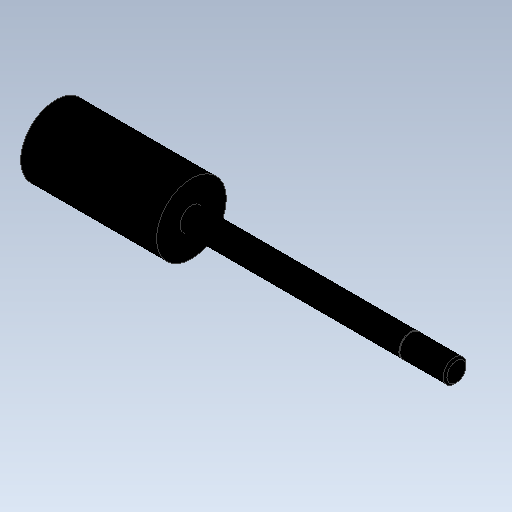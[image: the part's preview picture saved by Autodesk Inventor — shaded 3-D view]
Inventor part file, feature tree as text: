
AUTODESK INVENTOR PART (.ipt)
format: ipt  version: 2020 (Build 240168000, 168)  size: 123,904 bytes
history: native  units: mm (DEFAULTED — no unit token found)
features: other x70, revolve x3, sketch x3
ambient origin geometry x8: Origin, YZ Plane, XZ Plane, XY Plane, X Axis, Y Axis, Z Axis, Center Point
bodies: Solid1 (feature_tree)
feature tree (76):
  revolve  "Revolution1"  Angle=360.0deg
  revolve  "Revolution2"  [1 undecoded]
  revolve  "Revolution3"  [1 undecoded]
  other  "dia1_XY"
  other  "dia1_YZ"
  other  "dia1_ZX"
  other  "dia1_X"
  other  "dia1_Y"
  other  "dia1_Z"
  other  "dia1_Center"
  other  "dia12_XY"
  other  "dia12_YZ"
  other  "dia12_ZX"
  other  "dia12_X"
  other  "dia12_Y"
  other  "dia12_Z"
  other  "dia12_Center"
  other  "dia2_XY"
  other  "dia2_YZ"
  other  "dia2_ZX"
  other  "dia2_X"
  other  "dia2_Y"
  other  "dia2_Z"
  other  "dia2_Center"
  other  "dia22_XY"
  other  "dia22_YZ"
  other  "dia22_ZX"
  other  "dia22_X"
  other  "dia22_Y"
  other  "dia22_Z"
  other  "dia22_Center"
  other  "rl1_XY"
  other  "rl1_YZ"
  other  "rl1_ZX"
  other  "rl1_X"
  other  "rl1_Y"
  other  "rl1_Z"
  other  "rl1_Center"
  other  "rl2_XY"
  other  "rl2_YZ"
  other  "rl2_ZX"
  other  "rl2_X"
  other  "rl2_Y"
  other  "rl2_Z"
  other  "rl2_Center"
  other  "rod_cp_XY"
  other  "rod_cp_YZ"
  other  "rod_cp_ZX"
  other  "rod_cp_X"
  other  "rod_cp_Y"
  other  "rod_cp_Z"
  other  "rod_cp_Center"
  other  "thd1_XY"
  other  "thd1_YZ"
  other  "thd1_ZX"
  other  "thd1_X"
  other  "thd1_Y"
  other  "thd1_Z"
  other  "thd1_Center"
  other  "thd2_XY"
  other  "thd2_YZ"
  other  "thd2_ZX"
  other  "thd2_X"
  other  "thd2_Y"
  other  "thd2_Z"
  other  "thd2_Center"
  other  "to_rod_clevis_XY"
  other  "to_rod_clevis_YZ"
  other  "to_rod_clevis_ZX"
  other  "to_rod_clevis_X"
  other  "to_rod_clevis_Y"
  other  "to_rod_clevis_Z"
  other  "to_rod_clevis_Center"
  sketch  "Sketch_1"  dims[d0=360.0deg d1=360.0deg]
  sketch  "Sketch_3"  dims[d2=360.0deg]
  sketch  "Sketch_30"  dims[d3=0.0mm d4=0.0mm d5=0.0mm d6=0.0mm d7=0.0mm]
note: 2 required parameter values undecoded (feature->parameter linkage not recoverable at this tier; creation-order binding heuristic only, values carry confidence <= 0.55)
